# Revit family: HL_Трап для внутренних помещений_HL70G
name_source: partatom
category: Instalační zařizovací předměty
revit_build: Autodesk Revit 2016 (Build: 20161004_0715(x64)
units: mm (PartAtom-declared; Revit-internal decimal feet)

## family parameters
Bod výpočtu místnosti = Ano
Kóta kulaté spojky = Použít průměr
Nadpis OmniClass = Deck Waste Water Drains
Ořezat dutým tvarem při načtení = Ne
Sdílené = Ano
Typ součásti = Normální
Vždy vertikální = Ano
Založené na pracovní rovině = Ne
Číslo OmniClass = 23.70.50.21.24.14

## types (1)
- HL_Трап для внутренних помещений_HL70G
    EAN = 9003076001941
    Klíčová poznámka = HL70G
    Komentáře k typům = Трап для внутренних помещений DN75/110 горизонтальный с предохранительным затвором обратного потока воды и тремя входными отверстиями DN40/50, 150х150мм/137х137мм чугун
    Model = HL70G
    Popis = Трап для внутренних помещений
    Připojení CW = Ne
    Připojení HW = Ne
    Připojení odpadu = Ano
    Připojení ventilace = Ne
    URL = http://www.hutterer-lechner.com
    Výrobce = HL Hutterer & Lechner GmbH
    ВЕС = 2,892 kg
    ВЫСОТА МОНТАЖА = 213 mm
    МАКСИМАЛЬНАЯ НАГРУЗКА КЛАССА = A/L15 - 1,5 t
    МАТЕРИАЛ = PE
    НАСАДКА = 35-75 mm / 150 x 150 mm / GJL
    ПРИЁМНОЕ ОТВЕРСТИЕ = 3 x DN40/50
    ПРОИЗВОДИТЕЛЬНОСТЬ = 1,12 l/s
    РАЗМЕР = DN75/110
    РЕШЁТКА = 137x137mm/ GJL

## geometry (parser evidence)
native form markers: Sweep x41
no freeform markers — native parametric forms only
